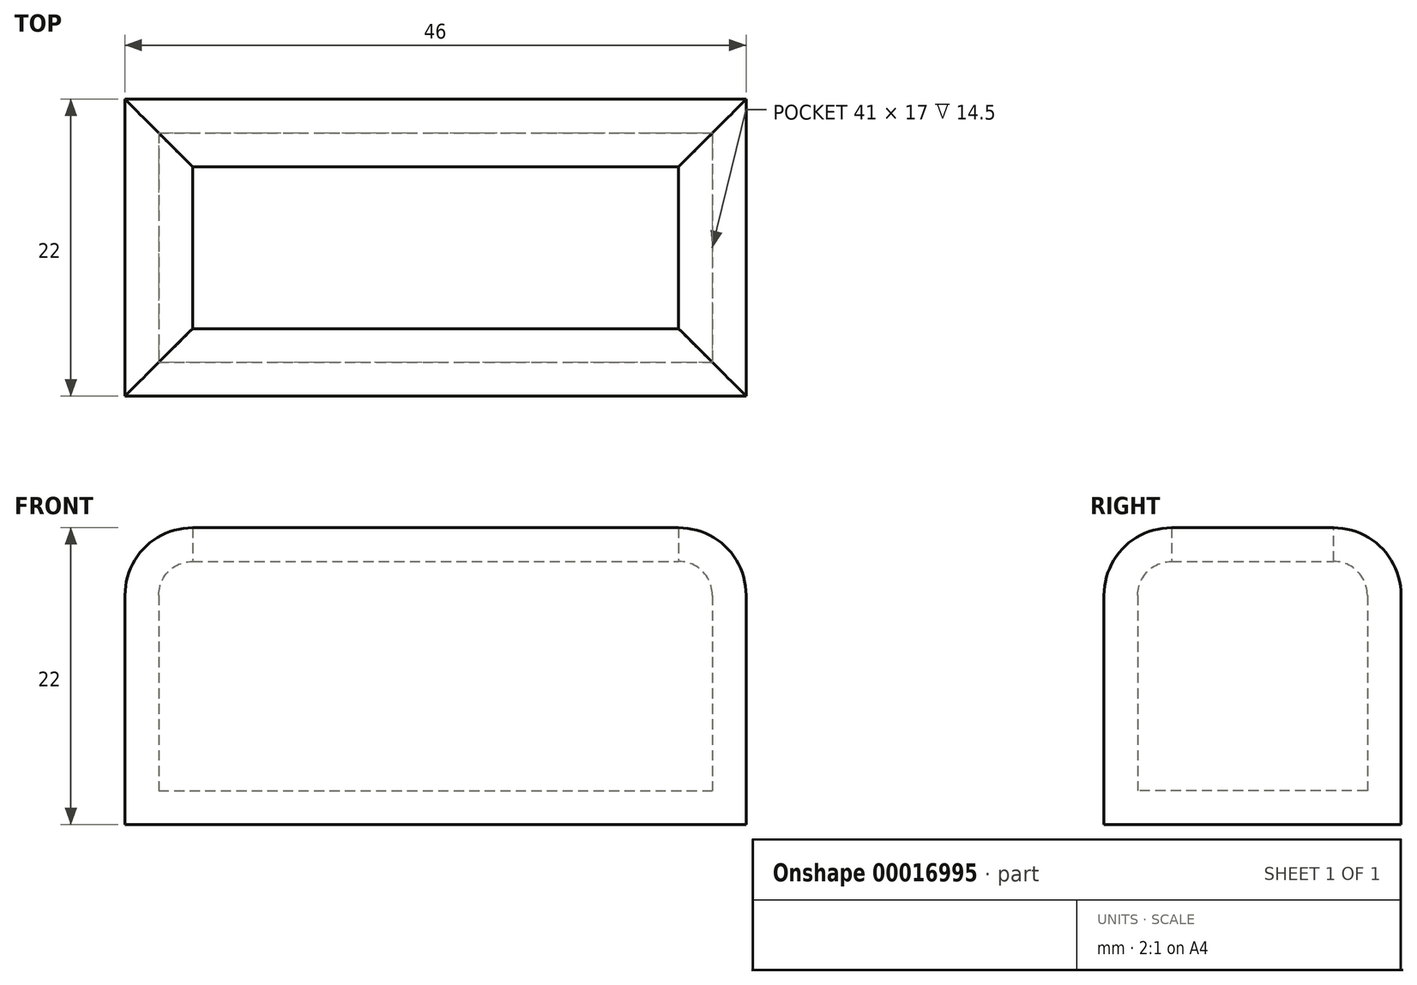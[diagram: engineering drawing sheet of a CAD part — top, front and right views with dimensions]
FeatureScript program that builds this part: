
annotation { "Feature Type Name" : "Feature", "Feature Type Description" : "" }
export const myFeature = defineFeature(function(context is Context, id is Id, definition is map)
    precondition{}
    {
        {
            var Q0;
            Q0=qCreatedBy(makeId("Top.planeOp"),FACE);
            var sketch = newSketch(context, id + "F0", { "sketchPlane" : qUnion([Q0])});
            skLineSegment(sketch, "E0.bottom", {"start": v(-10, 6.17) * mm, "end": v(36, 6.17) * mm});
            skLineSegment(sketch, "E0.top", {"start": v(-10, -15.83) * mm, "end": v(36, -15.83) * mm});
            skLineSegment(sketch, "E0.left", {"start": v(-10, 6.17) * mm, "end": v(-10, -15.83) * mm});
            skLineSegment(sketch, "E0.right", {"start": v(36, 6.17) * mm, "end": v(36, -15.83) * mm});
            skSolve(sketch);
        }
        {
            var Q0;
            Q0=makeQuery(id+"F0.imprint","IMPRINT",FACE,{"disambiguationData":[TD([[makeQuery(id+"F0.imprint","IMPRINT",EDGE,{"derivedFrom":sQuery(id+"F0.wireOp",EDGE,"E0.bottom")}),-1.0]])]});
            extrude(context, id + "F1", {"entities" : qUnion([Q0]), "depth" : 22 * mm});
        }
        {
            var Q0;
            Q0=makeQuery(id+"F1.opExtrude","CAP_EDGE",EDGE,{"disambiguationData":[OSD([sQuery(id+"F0.wireOp",EDGE,"E0.bottom")])],"isStart":false});
            var Q1;
            Q1=makeQuery(id+"F1.opExtrude","CAP_EDGE",EDGE,{"disambiguationData":[OSD([sQuery(id+"F0.wireOp",EDGE,"E0.left")])],"isStart":false});
            var Q2;
            Q2=makeQuery(id+"F1.opExtrude","CAP_EDGE",EDGE,{"disambiguationData":[OSD([sQuery(id+"F0.wireOp",EDGE,"E0.top")])],"isStart":false});
            var Q3;
            Q3=makeQuery(id+"F1.opExtrude","CAP_EDGE",EDGE,{"disambiguationData":[OSD([sQuery(id+"F0.wireOp",EDGE,"E0.right")])],"isStart":false});
            fillet(context, id + "F2", {"entities" : qUnion([Q0, Q1, Q2, Q3]), "radius" : 5 * mm, "tangentPropagation" : true, "allowEdgeOverflow" : false});
        }
        {
            var Q0;
            Q0=makeQuery(id+"F1.opExtrude","CAP_FACE",FACE,{"disambiguationData":[OSD([sQuery(id+"F0.wireOp",EDGE,"E0.bottom"),sQuery(id+"F0.wireOp",EDGE,"E0.top"),sQuery(id+"F0.wireOp",EDGE,"E0.left"),sQuery(id+"F0.wireOp",EDGE,"E0.right")])],"isStart":false});
            shell(context, id + "F3", {"entities" : qUnion([Q0]), "thickness" : 2.5 * mm});
        }
    });
